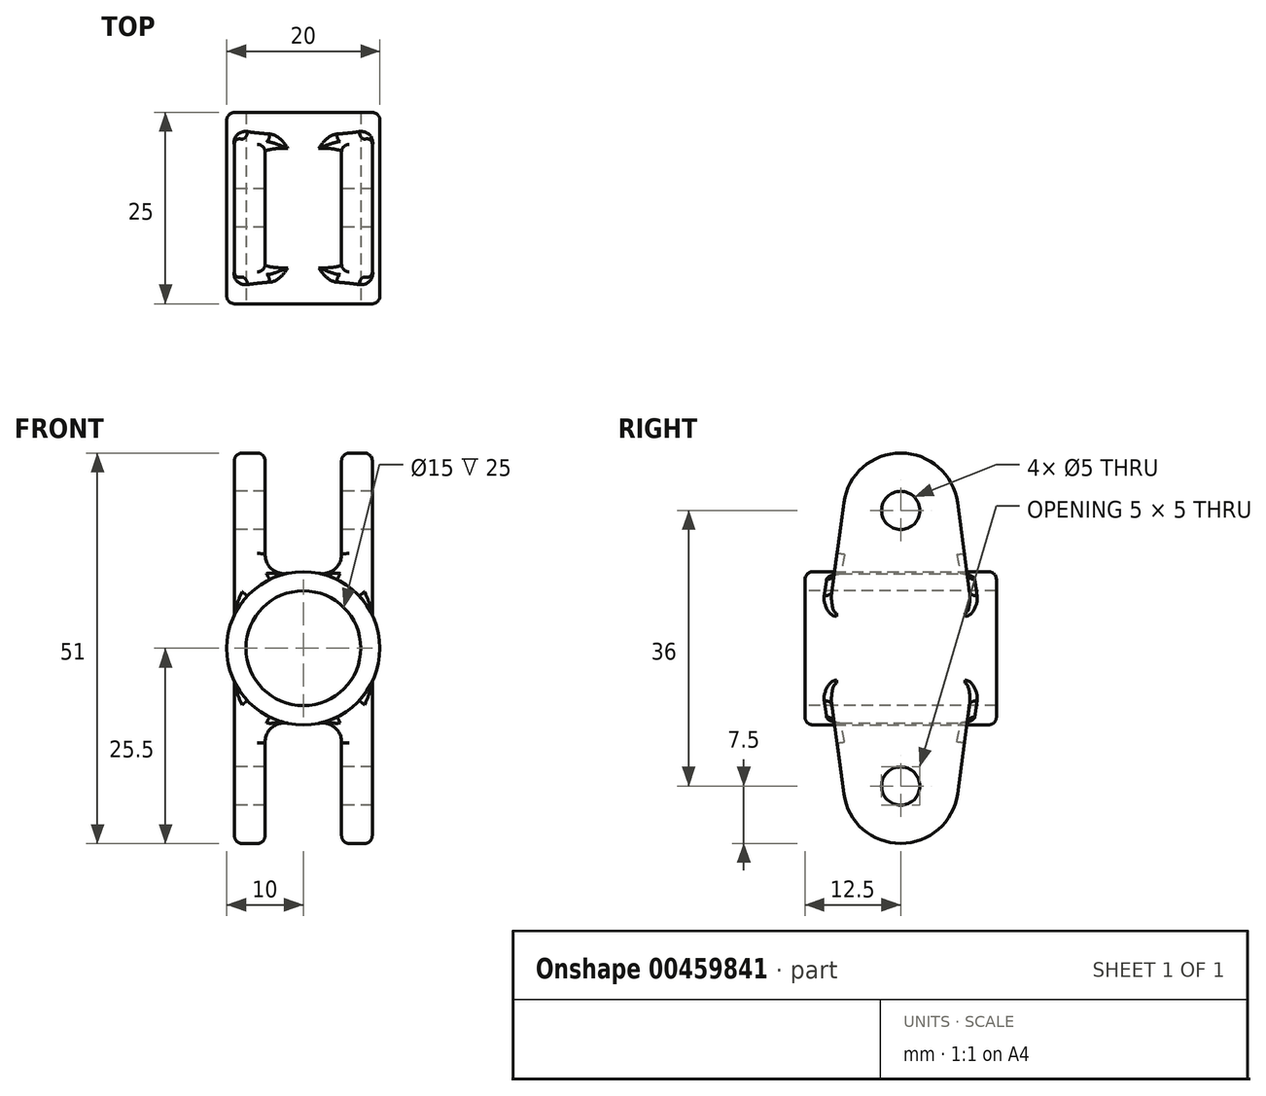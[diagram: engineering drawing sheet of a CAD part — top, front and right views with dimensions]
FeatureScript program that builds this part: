
annotation { "Feature Type Name" : "Feature", "Feature Type Description" : "" }
export const myFeature = defineFeature(function(context is Context, id is Id, definition is map)
    precondition{}
    {
        {
            var Q0;
            Q0=qCreatedBy(makeId("Front.planeOp"),FACE);
            var sketch = newSketch(context, id + "F0", { "sketchPlane" : qUnion([Q0])});
            skCircle(sketch, "E0", {"center": v(0, 0) * mm, "radius": 10 * mm});
            skSolve(sketch);
        }
        {
            var Q0;
            Q0 = qSketchRegion(id + "F0", true);
            extrude(context, id + "F1", {"entities" : qUnion([Q0]), "depth" : 25 * mm, "offsetDistance" : 25 * mm});
        }
        {
            var Q0;
            Q0=qCreatedBy(makeId("Right.planeOp"),FACE);
            var sketch = newSketch(context, id + "F2", { "sketchPlane" : qUnion([Q0])});
            skLineSegment(sketch, "E1", {"start": v(-22.5, 0) * mm, "end": v(-19.93, 19) * mm});
            skCircle(sketch, "E2", {"center": v(-12.5, 18) * mm, "radius": 7.5 * mm});
            skCircle(sketch, "E3", {"center": v(-12.5, 18) * mm, "radius": 2.5 * mm});
            skLineSegment(sketch, "E4", {"start": v(-12.5, 18) * mm, "end": v(-12.5, 0) * mm});
            skLineSegment(sketch, "E5", {"start": v(-22.5, 0) * mm, "end": v(-12.5, 0) * mm});
            skLineSegment(sketch, "E6.MirrorCS", {"start": v(-2.5, 0) * mm, "end": v(-5.07, 19) * mm});
            skLineSegment(sketch, "E7.MirrorCS", {"start": v(-2.5, 0) * mm, "end": v(-12.5, 0) * mm});
            skLineSegment(sketch, "E8.MirrorCS", {"start": v(-22.5, 0) * mm, "end": v(-19.93, -19) * mm});
            skLineSegment(sketch, "E9.MirrorCS", {"start": v(-12.5, -18) * mm, "end": v(-12.5, 0) * mm});
            skCircle(sketch, "E10.MirrorC", {"center": v(-12.5, -18) * mm, "radius": 7.5 * mm});
            skLineSegment(sketch, "E11.MirrorCS", {"start": v(-2.5, 0) * mm, "end": v(-5.07, -19) * mm});
            skCircle(sketch, "E12.MirrorC", {"center": v(-12.5, -18) * mm, "radius": 2.5 * mm});
            skSolve(sketch);
        }
        {
            var Q0;
            Q0 = qSketchRegion(id + "F2", true);
            extrude(context, id + "F3", {"entities" : qUnion([Q0]), "operationType" : NewBodyOperationType.ADD, "endBound" : BoundingType.SYMMETRIC, "depth" : 18 * mm, "offsetDistance" : 25 * mm});
        }
        {
            var Q0;
            Q0=makeQuery(id+"F1.opExtrude","CAP_FACE",FACE,{"disambiguationData":[OSD([sQuery(id+"F0.wireOp",EDGE,"E0")])],"isStart":false});
            var sketch = newSketch(context, id + "F4", { "sketchPlane" : qUnion([Q0])});
            skCircle(sketch, "E13", {"center": v(0, 0) * mm, "radius": 10 * mm});
            skLineSegment(sketch, "E14", {"start": v(-5, 8.66) * mm, "end": v(-5, 33.66) * mm});
            skLineSegment(sketch, "E15", {"start": v(-5, 33.66) * mm, "end": v(0, 33.66) * mm});
            skLineSegment(sketch, "E16", {"start": v(0, 33.66) * mm, "end": v(0, 10) * mm});
            skLineSegment(sketch, "E17", {"start": v(-7.6, 0) * mm, "end": v(7.88, 0) * mm});
            skLineSegment(sketch, "E18.MirrorCS", {"start": v(5, 33.66) * mm, "end": v(0, 33.66) * mm});
            skLineSegment(sketch, "E19.MirrorCS", {"start": v(5, 8.66) * mm, "end": v(5, 33.66) * mm});
            skLineSegment(sketch, "E20.MirrorCS", {"start": v(-5, -8.66) * mm, "end": v(-5, -33.66) * mm});
            skLineSegment(sketch, "E21.MirrorCS", {"start": v(-5, -33.66) * mm, "end": v(0, -33.66) * mm});
            skLineSegment(sketch, "E22.MirrorCS", {"start": v(5, -8.66) * mm, "end": v(5, -33.66) * mm});
            skLineSegment(sketch, "E23.MirrorCS", {"start": v(5, -33.66) * mm, "end": v(0, -33.66) * mm});
            skCircle(sketch, "E24", {"center": v(0, 0) * mm, "radius": 7.5 * mm});
            skSolve(sketch);
        }
        {
            var Q0;
            {var subQ1=sQuery(id+"F4.wireOp",EDGE,"E20.MirrorCS");Q0=makeQuery(id+"F4.imprint","IMPRINT",FACE,{"disambiguationData":[TD([[makeQuery(id+"F4.imprint","IMPRINT",EDGE,{"derivedFrom":subQ1}),1.0]])]});}
            var Q1;
            {var subQ0=sQuery(id+"F4.wireOp",EDGE,"E16");Q1=makeQuery(id+"F4.imprint","IMPRINT",FACE,{"disambiguationData":[TD([[makeQuery(id+"F4.imprint","IMPRINT",EDGE,{"derivedFrom":subQ0}),1.0]])]});}
            var Q2;
            {var subQ0=sQuery(id+"F4.wireOp",EDGE,"E14");Q2=makeQuery(id+"F4.imprint","IMPRINT",FACE,{"disambiguationData":[TD([[makeQuery(id+"F4.imprint","IMPRINT",EDGE,{"derivedFrom":subQ0}),-1.0]])]});}
            var Q3;
            {var subQ0=sQuery(id+"F4.wireOp",EDGE,"E24");var subQ1=sQuery(id+"F4.wireOp",EDGE,"E17");var subQ2=makeQuery(id+"F4.imprint","INTERSECT",VERTEX,{"disambiguationData":[OD(0.0)],"derivedFrom":[subQ1,subQ0]});Q3=makeQuery(id+"F4.imprint","IMPRINT",FACE,{"disambiguationData":[TD([[makeQuery(id+"F4.imprint","IMPRINT",EDGE,{"disambiguationData":[TD([[subQ2,-1.0]])],"derivedFrom":subQ1}),1.0]])]});}
            var Q4;
            {var subQ0=sQuery(id+"F4.wireOp",EDGE,"E24");var subQ1=sQuery(id+"F4.wireOp",EDGE,"E17");var subQ2=makeQuery(id+"F4.imprint","INTERSECT",VERTEX,{"disambiguationData":[OD(0.0)],"derivedFrom":[subQ1,subQ0]});Q4=makeQuery(id+"F4.imprint","IMPRINT",FACE,{"disambiguationData":[TD([[makeQuery(id+"F4.imprint","IMPRINT",EDGE,{"disambiguationData":[TD([[subQ2,-1.0]])],"derivedFrom":subQ1}),-1.0]])]});}
            extrude(context, id + "F5", {"entities" : qUnion([Q0, Q1, Q2, Q3, Q4]), "operationType" : NewBodyOperationType.REMOVE, "oppositeDirection" : true, "depth" : 25 * mm, "offsetDistance" : 25 * mm});
        }
        {
            var Q0;
            Q0=makeQuery(id+"F5.boolean.opBoolean","COPY",EDGE,{"derivedFrom":makeQuery(id+"F5.opExtrude","SWEPT_EDGE",EDGE,{"disambiguationData":[OSD([sQuery(id+"F4.wireOp",EDGE,"E13"),sQuery(id+"F4.wireOp",EDGE,"E14")])]})});
            var Q1;
            Q1=makeQuery(id+"F5.boolean.opBoolean","COPY",EDGE,{"derivedFrom":makeQuery(id+"F5.opExtrude","SWEPT_EDGE",EDGE,{"disambiguationData":[OSD([sQuery(id+"F4.wireOp",EDGE,"E13"),sQuery(id+"F4.wireOp",EDGE,"E19.MirrorCS")])]})});
            var Q2;
            Q2=makeQuery(id+"F5.boolean.opBoolean","COPY",EDGE,{"derivedFrom":makeQuery(id+"F5.opExtrude","SWEPT_EDGE",EDGE,{"disambiguationData":[OSD([sQuery(id+"F4.wireOp",EDGE,"E13"),sQuery(id+"F4.wireOp",EDGE,"E20.MirrorCS")])]})});
            var Q3;
            Q3=makeQuery(id+"F5.boolean.opBoolean","COPY",EDGE,{"derivedFrom":makeQuery(id+"F5.opExtrude","SWEPT_EDGE",EDGE,{"disambiguationData":[OSD([sQuery(id+"F4.wireOp",EDGE,"E13"),sQuery(id+"F4.wireOp",EDGE,"E22.MirrorCS")])]})});
            fillet(context, id + "F6", {"entities" : qUnion([Q0, Q1, Q2, Q3]), "radius" : 2.5 * mm, "tangentPropagation" : true, "allowEdgeOverflow" : false});
        }
        {
            var Q0;
            {var subQ1=sQuery(id+"F2.wireOp",EDGE,"E10.MirrorC");Q0=makeQuery(id+"F5.boolean.opBoolean","SPLIT",FACE,{"disambiguationData":[TD([makeQuery(id+"F5.opExtrude","SWEPT_FACE",FACE,{"disambiguationData":[OSD([sQuery(id+"F4.wireOp",EDGE,"E22.MirrorCS")])]})])],"derivedFrom":makeQuery(id+"F3.opExtrude","SWEPT_FACE",FACE,{"disambiguationData":[OSD([subQ1])]})});}
            var Q1;
            {var subQ1=sQuery(id+"F2.wireOp",EDGE,"E10.MirrorC");Q1=makeQuery(id+"F5.boolean.opBoolean","SPLIT",FACE,{"disambiguationData":[TD([makeQuery(id+"F5.opExtrude","SWEPT_FACE",FACE,{"disambiguationData":[OSD([sQuery(id+"F4.wireOp",EDGE,"E20.MirrorCS")])]})])],"derivedFrom":makeQuery(id+"F3.opExtrude","SWEPT_FACE",FACE,{"disambiguationData":[OSD([subQ1])]})});}
            var Q2;
            {var subQ2=sQuery(id+"F2.wireOp",EDGE,"E2");Q2=makeQuery(id+"F5.boolean.opBoolean","SPLIT",FACE,{"disambiguationData":[TD([makeQuery(id+"F5.opExtrude","SWEPT_FACE",FACE,{"disambiguationData":[OSD([sQuery(id+"F4.wireOp",EDGE,"E14")])]})])],"derivedFrom":makeQuery(id+"F3.opExtrude","SWEPT_FACE",FACE,{"disambiguationData":[OSD([subQ2])]})});}
            var Q3;
            {var subQ2=sQuery(id+"F2.wireOp",EDGE,"E2");Q3=makeQuery(id+"F5.boolean.opBoolean","SPLIT",FACE,{"disambiguationData":[TD([makeQuery(id+"F5.opExtrude","SWEPT_FACE",FACE,{"disambiguationData":[OSD([sQuery(id+"F4.wireOp",EDGE,"E19.MirrorCS")])]})])],"derivedFrom":makeQuery(id+"F3.opExtrude","SWEPT_FACE",FACE,{"disambiguationData":[OSD([subQ2])]})});}
            var Q4;
            {var subQ0=sQuery(id+"F4.wireOp",EDGE,"E13");var subQ1=makeQuery(id+"F4.imprint","INTERSECT",VERTEX,{"derivedFrom":[subQ0,sQuery(id+"F4.wireOp",EDGE,"E16")]});Q4=makeQuery(id+"F5.boolean.opBoolean","MERGE",FACE,{"derivedFrom":[makeQuery(id+"F1.opExtrude","SWEPT_FACE",FACE,{"disambiguationData":[OSD([sQuery(id+"F0.wireOp",EDGE,"E0")])]}),makeQuery(id+"F5.opExtrude","SWEPT_FACE",FACE,{"disambiguationData":[OSD([subQ0]),TDD([makeQuery(id+"F4.imprint","IMPRINT",EDGE,{"disambiguationData":[TD([[subQ1,1.0]])],"derivedFrom":subQ0}),makeQuery(id+"F4.imprint","IMPRINT",EDGE,{"disambiguationData":[TD([[makeQuery(id+"F4.imprint","INTERSECT",VERTEX,{"derivedFrom":[subQ0,sQuery(id+"F4.wireOp",EDGE,"E14")]}),1.0]])],"derivedFrom":subQ0})])]}),makeQuery(id+"F5.opExtrude","SWEPT_FACE",FACE,{"disambiguationData":[OSD([subQ0]),TDD([makeQuery(id+"F4.imprint","IMPRINT",EDGE,{"disambiguationData":[TD([[makeQuery(id+"F4.imprint","INTERSECT",VERTEX,{"derivedFrom":[subQ0,sQuery(id+"F4.wireOp",EDGE,"E20.MirrorCS")]}),-1.0]])],"derivedFrom":subQ0})])]})]});}
            fillet(context, id + "F7", {"entities" : qUnion([Q0, Q1, Q2, Q3, Q4]), "radius" : 1 * mm, "tangentPropagation" : true, "allowEdgeOverflow" : false});
        }
    });
